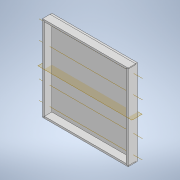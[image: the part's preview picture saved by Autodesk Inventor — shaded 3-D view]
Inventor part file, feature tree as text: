
AUTODESK INVENTOR PART (.ipt)
format: ipt  version: 2022 (Build 260153000, 153)  size: 181,248 bytes
history: native  units: mm
features: sketch x5, extrude x4, other x4, plane x3, projected_geometry x3, boolean_combine x2, mirror x2, shell x1
ambient origin geometry x8: Origin, YZ Plane, XZ Plane, XY Plane, X Axis, Y Axis, Z Axis, Center Point
bodies: Solid3 (feature_tree), Solid4 (feature_tree)
feature tree (24):
  extrude  "Extrusion3"  Depth=292.1mm
  sketch  "Sketch2"  dims[d15=88.9mm d16=88.9mm]
  shell  "Shell1"  Thickness=31.75mm
  sketch  "Sketch3"  dims[d17=6.35mm d20=25.4mm]
  other  "Work Axis3"
  other  "Work Axis4"
  other  "Work Axis5"
  other  "Work Axis6"
  sketch  "Sketch6"  dims[d24=25.4mm d25=7.271042mm d26=6.35mm d27=0.0mm d28=6.5mm d42=10.0mm d43=0.0mm d44=10.0mm d45=0.0mm]
  extrude  "Extrusion6"  Depth=88.9mm
  extrude  "Extrusion7"  Depth=25.4mm
  boolean_combine  "Combine1"
  boolean_combine  "Combine2"
  plane  "Work Plane3"
  extrude  "Extrusion4"  Depth=88.9mm
  plane  "Work Plane1"
  plane  "Work Plane2"
  mirror  "Mirror1"
  mirror  "Mirror2"
  sketch  "Sketch1"  dims[d11=292.1mm d12=292.1mm d13=31.75mm d14=0.0mm]
  projected_geometry  "Projected Loop1"
  sketch  "Sketch4"  dims[d22=88.9mm d23=88.9mm]
  projected_geometry  "Projected Loop2"
  projected_geometry  "Projected Loop3"
